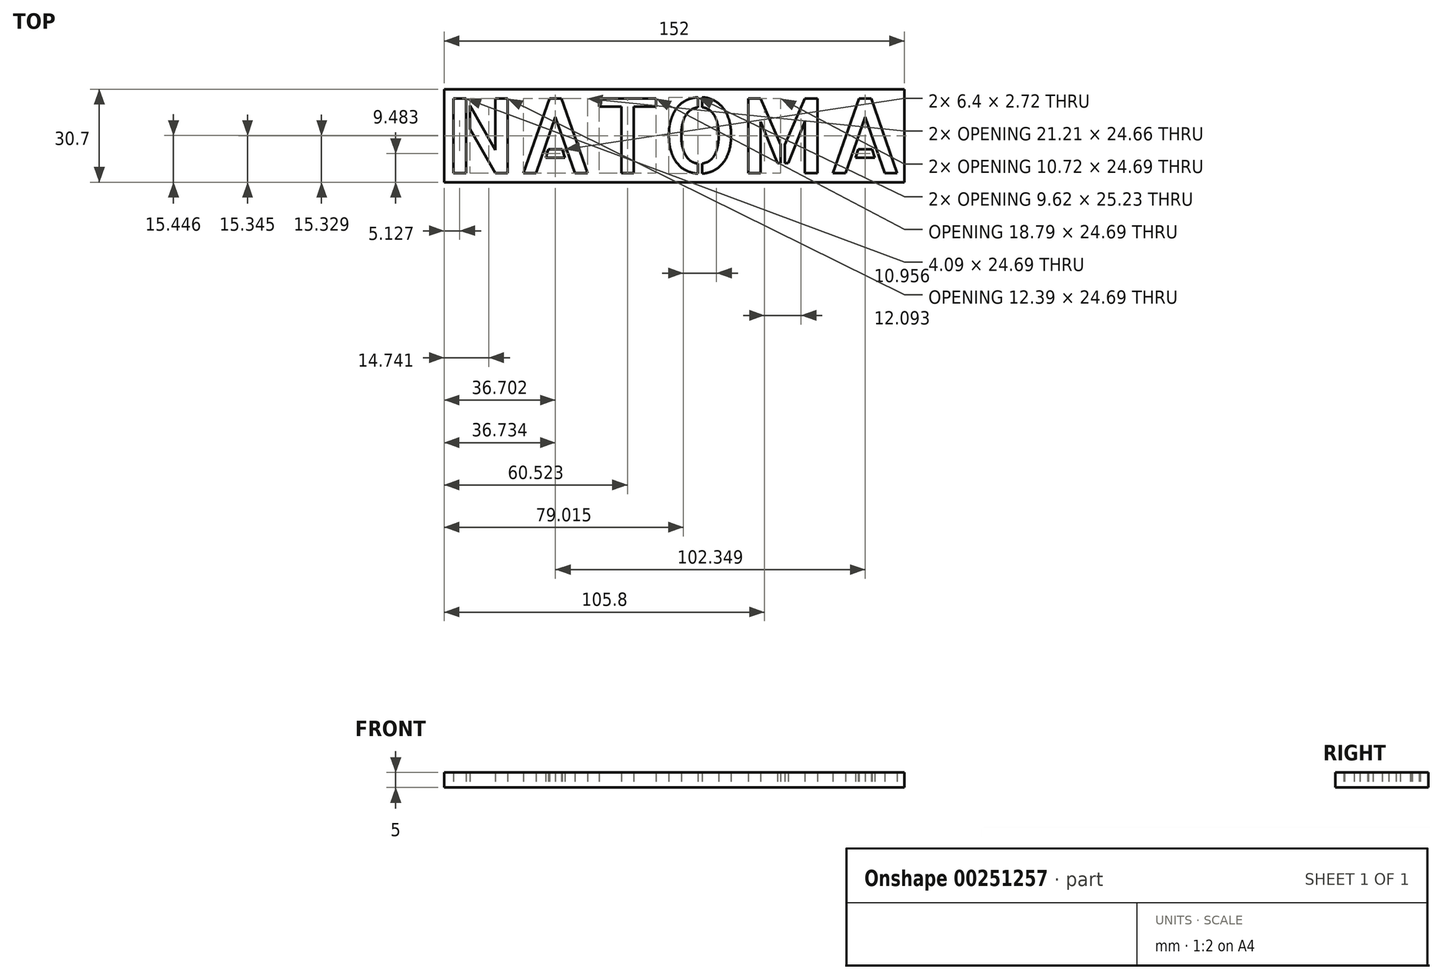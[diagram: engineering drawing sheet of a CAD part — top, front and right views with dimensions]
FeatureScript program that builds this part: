
annotation { "Feature Type Name" : "Feature", "Feature Type Description" : "" }
export const myFeature = defineFeature(function(context is Context, id is Id, definition is map)
    precondition{}
    {
        {
            var Q0;
            Q0=qCreatedBy(makeId("Top.planeOp"),FACE);
            var sketch = newSketch(context, id + "F0", { "sketchPlane" : qUnion([Q0])});
            skText(sketch, "E0", { "text": "NATOMA", "fontName": "AllertaStencil-Regular.ttf"});
            skLineSegment(sketch, "E1.bottom", {"start": v(76, -15.35) * mm, "end": v(-76, -15.35) * mm});
            skLineSegment(sketch, "E1.top", {"start": v(76, 15.35) * mm, "end": v(-76, 15.35) * mm});
            skLineSegment(sketch, "E1.left", {"start": v(76, -15.35) * mm, "end": v(76, 15.35) * mm});
            skLineSegment(sketch, "E1.right", {"start": v(-76, -15.35) * mm, "end": v(-76, 15.35) * mm});
            skPoint(sketch, "E1.middle", {"position": v(0, 0) * mm});
            const initialGuessF0  = {"E0": [-0.076, -0.01235, 1, 0, 0.0247]};
            skSetInitialGuess(sketch, initialGuessF0);
            skSolve(sketch);
        }
        {
            var Q0;
            Q0 = qSketchRegion(id + "F0", true);
            extrude(context, id + "F1", {"entities" : qUnion([Q0]), "depth" : 5 * mm});
        }
    });
